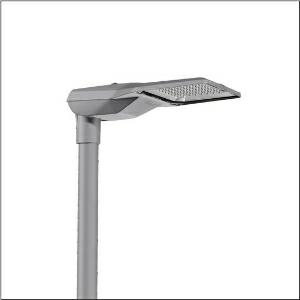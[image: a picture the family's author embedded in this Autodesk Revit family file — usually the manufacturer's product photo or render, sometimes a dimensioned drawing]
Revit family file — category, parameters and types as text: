
# Revit family: streetlight_sl_21_midi___stw1_0a_5xe3e43s08nb_fb33
name_source: partatom
category: Lighting Fixtures
units: mm (PartAtom-declared; Revit-internal decimal feet)

## family parameters
Cut with Voids When Loaded = No
Host = Face
Light Source = No
Part Type = Normal
Room Calculation Point = No
Round Connector Dimension = Use Diameter
Shared = No

## types (1)
- --- (1 x LED, 23710 lm, 151.2 W, 4000K)
    Apparent Load = 151 VA
    CIE Flux Codes = 39 75 98 100 100
    Color Rendering = 70
    Color Temperature = 4000K
    Default Elevation = 1800 mm
    Description = Streetlight SL 21 midi, mast luminaire, primary light control with lens, of PMMA, primary optical cover: cover, of toughened safety glass, transparent, light distribution: STW1.0a, light emission: direct distribution, primary light characteristic: asymmetric, installation type: side-entry, post-top, LED, High Power LED, rated luminous flux: 23.710lm, luminous efficacy: 157lm/W, light colour: 740, colour temperature: 4000K, control gear: D4i, control: overheat protection, constant luminous flux control, time-dependent luminous flux control, flexible luminous flux parameterisation, pre-setting: logarithmic dimming characteristic, mains connection: 230..240V, AC, 50/60Hz, start of lifetime: 151W, end of service life: 157W, reduction: 70W, luminaire housing, of diecast aluminium, powder-coated, Siteco® metallic grey (DB 702S), corrosivity category C5 mid according to DIN EN ISO 12944, please order mast flange separately, inclination adjustable: 0°, 5°, 10°, 15°, sealing non-destructively replaceable, multi-level sealing system, length: 644mm, width: 335mm, height: 110mm, mast flange for spigot size: 42mm (side-entry): 5XC10008XM4, 60/48mm (side-entry/post-top): 5XC10108XM2, 76/60mm (side-entry/post-top): 5XC10108XM1, mounting height: 4..8m, Smart Interface above, protection rating (complete): IP66, insulation class (complete): insulation class II (safety insulation), certification: CE, ENEC, ENEC+, VDE, impact resistance: IK10, permissible operating ambient temperature for outdoor applications: -40..+50°C, standard-compliant lighting for roads and squares, packaging unit: 1 piece

Light Distribution: STW1.0a
    Height = 111 mm
    Lamp = 1 x LED
    Lamp Light Flux = 23710 lm
    Lamp Power = 151.2 W
    Lamp count = 1
    Length = 644 mm
    Luminous efficacy = 157 lm/W
    Manufacturer = Siteco
    ModVariant = No
    Model = 5XE3E43S08NB
    Number of Poles = 1
    OnlyDefault = Yes
    Power Factor = 1
    Product Name = Streetlight SL 21 midi | STW1.0a
    Product group = mast luminaire | pylon top
    ProductGroupID = 6100
    Protection Class = Protection class II
    Protection Degree = IP 66
    RLX_Detail_Level = 1
    RLX_Emergency_Light_Flux = 0 lm
    RLX_Emergency_Type = 0
    RLX_Emergency_Type_DB = No
    RlxData = <blob elided: 27025 chars, md5=fc43e72d>
    Socket = socket
    Standby Power = 0 W
    System Light Flux = 23710 lm
    System Power = 151 W
    Type Comments = factory setting: luminous flux: 100 % | dim-lin: 254 | 802 mA
    Type Image = l_1004302.jpg
    URL = http://relux.com
    VarID = @adj_169648
    Voltage = 0 V
    Weight = 0.00 kg
    Width = 336 mm

## geometry (parser evidence)
native form markers: Blend x4, Sweep x11
no freeform markers — native parametric forms only
